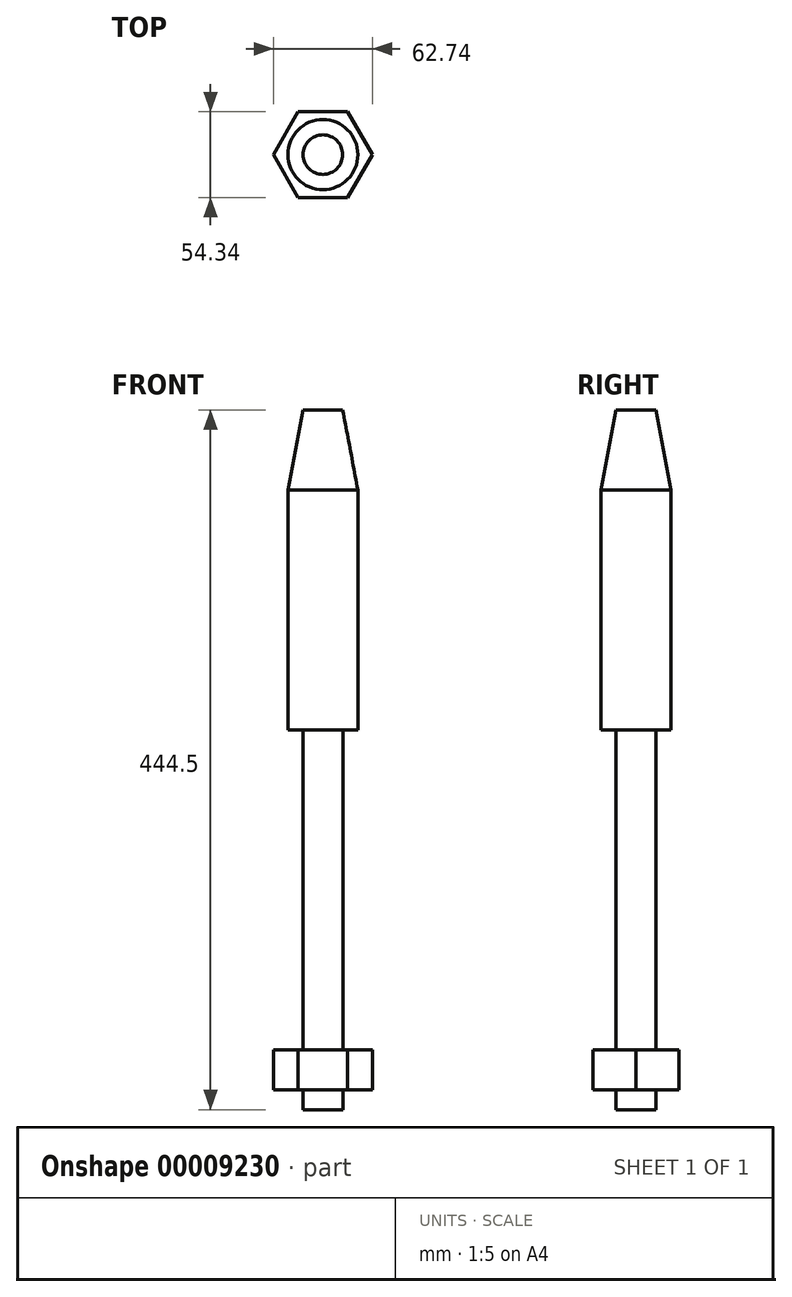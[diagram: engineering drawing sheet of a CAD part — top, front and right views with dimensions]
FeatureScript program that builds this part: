
annotation { "Feature Type Name" : "Feature", "Feature Type Description" : "" }
export const myFeature = defineFeature(function(context is Context, id is Id, definition is map)
    precondition{}
    {
        {
            var Q0;
            Q0=qCreatedBy(makeId("Top.planeOp"),FACE);
            var sketch = newSketch(context, id + "F0", { "sketchPlane" : qUnion([Q0])});
            skCircle(sketch, "E0", {"center": v(0, 0) * mm, "radius": 12.7 * mm});
            skSolve(sketch);
        }
        {
            var Q0;
            Q0 = qSketchRegion(id + "F0", true);
            extrude(context, id + "F1", {"entities" : qUnion([Q0]), "oppositeDirection" : true, "depth" : 241.3 * mm});
        }
        {
            var Q0;
            Q0=qCreatedBy(makeId("Top.planeOp"),FACE);
            var sketch = newSketch(context, id + "F2", { "sketchPlane" : qUnion([Q0])});
            skCircle(sketch, "E1", {"center": v(0, 0) * mm, "radius": 22.23 * mm});
            skSolve(sketch);
        }
        {
            var Q0;
            Q0 = qSketchRegion(id + "F2", true);
            extrude(context, id + "F3", {"entities" : qUnion([Q0]), "operationType" : NewBodyOperationType.ADD, "depth" : 203.2 * mm});
        }
        {
            var Q0;
            Q0=makeQuery(id+"F3.opExtrude","CAP_EDGE",EDGE,{"disambiguationData":[OSD([sQuery(id+"F2.wireOp",EDGE,"E1")])],"isStart":false});
            chamfer(context, id + "F4", {"entities" : qUnion([Q0]), "chamferType" : ChamferType.TWO_OFFSETS, "width1" : 9.65 * mm, "oppositeDirection" : false, "width2" : 50.8 * mm, "tangentPropagation" : true});
        }
        {
            var Q0;
            Q0=qCreatedBy(makeId("Top.planeOp"),FACE);
            cPlane(context, id + "F5", {"entities" : qUnion([Q0]), "cplaneType" : CPlaneType.OFFSET, "offset" : 203.2 * mm, "oppositeDirection" : true, "width" : 152.4 * mm, "height" : 152.4 * mm});
        }
        {
            var Q0;
            Q0=qCreatedBy(id+"F5.planeOp",FACE);
            var sketch = newSketch(context, id + "F6", { "sketchPlane" : qUnion([Q0])});
            skCircle(sketch, "E2.cCircle", {"center": v(0, 0) * mm, "radius": 27.17 * mm, "construction": true});
            skLineSegment(sketch, "E2.0", {"start": v(-15.68, 27.17) * mm, "end": v(15.68, 27.17) * mm});
            skLineSegment(sketch, "E2.1", {"start": v(15.68, 27.17) * mm, "end": v(31.37, 0) * mm});
            skLineSegment(sketch, "E2.2", {"start": v(31.37, 0) * mm, "end": v(15.68, -27.17) * mm});
            skLineSegment(sketch, "E2.3", {"start": v(15.68, -27.17) * mm, "end": v(-15.68, -27.17) * mm});
            skLineSegment(sketch, "E2.4", {"start": v(-15.68, -27.17) * mm, "end": v(-31.37, 0) * mm});
            skLineSegment(sketch, "E2.5", {"start": v(-31.37, 0) * mm, "end": v(-15.68, 27.17) * mm});
            skPoint(sketch, "E2.0.midPoint", {"position": v(0, 27.17) * mm});
            skSolve(sketch);
        }
        {
            var Q0;
            Q0 = qSketchRegion(id + "F6", true);
            extrude(context, id + "F7", {"entities" : qUnion([Q0]), "operationType" : NewBodyOperationType.ADD, "oppositeDirection" : true, "depth" : 25.4 * mm});
        }
    });
